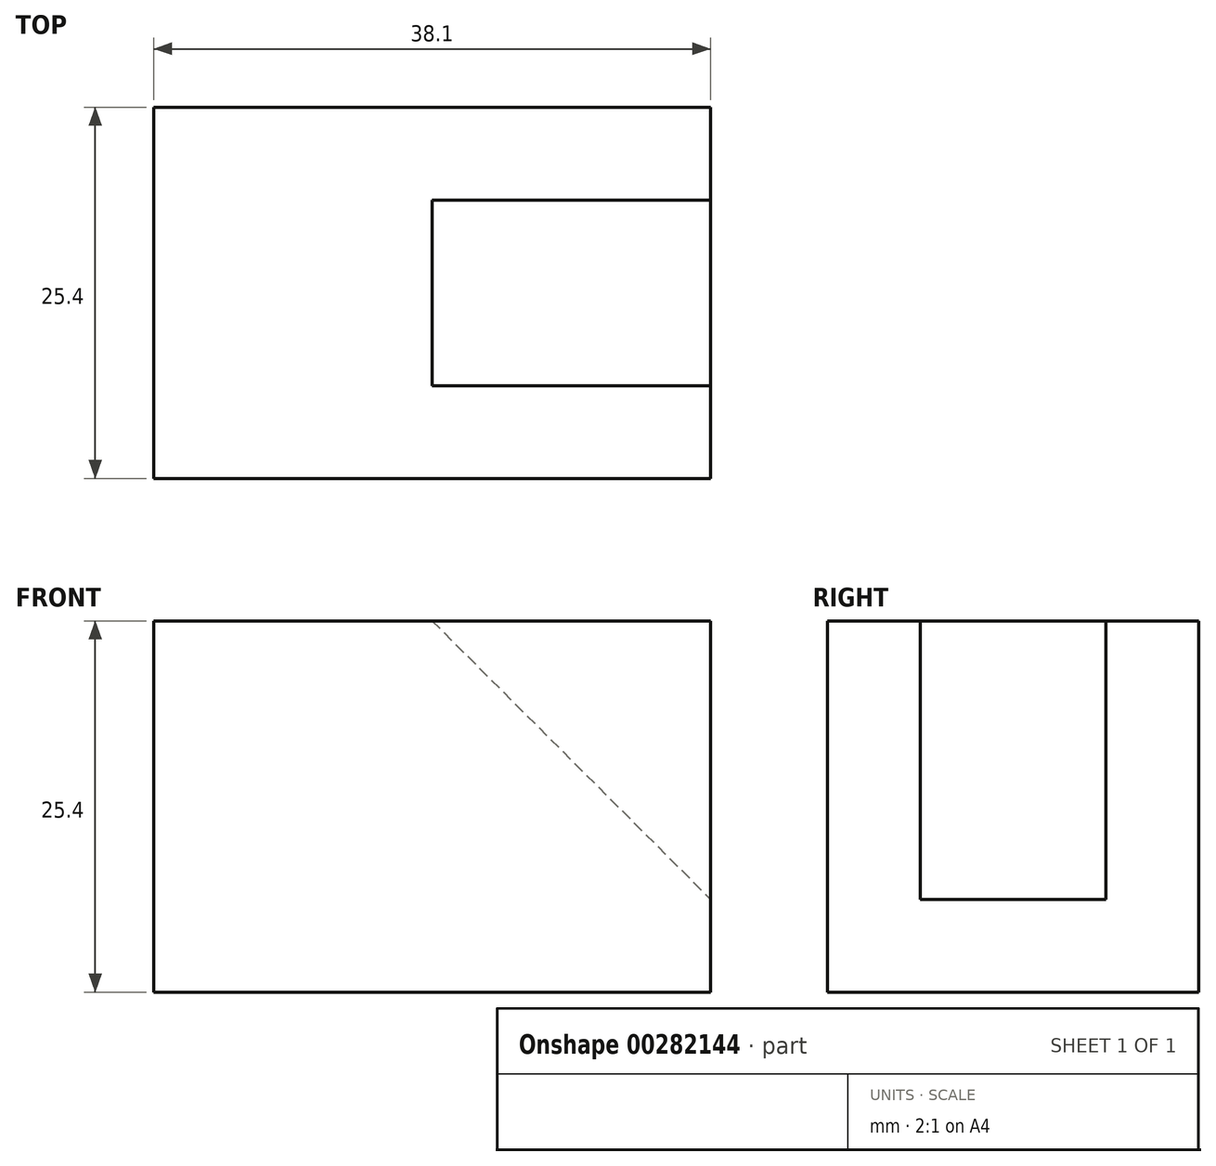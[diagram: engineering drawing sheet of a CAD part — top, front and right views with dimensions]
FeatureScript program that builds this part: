
annotation { "Feature Type Name" : "Feature", "Feature Type Description" : "" }
export const myFeature = defineFeature(function(context is Context, id is Id, definition is map)
    precondition{}
    {
        {
            var Q0;
            Q0=qCreatedBy(makeId("Front.planeOp"),FACE);
            var sketch = newSketch(context, id + "F0", { "sketchPlane" : qUnion([Q0])});
            skLineSegment(sketch, "E0.bottom", {"start": v(0, 0) * mm, "end": v(38.1, 0) * mm});
            skLineSegment(sketch, "E0.top", {"start": v(0, 25.4) * mm, "end": v(38.1, 25.4) * mm});
            skLineSegment(sketch, "E0.left", {"start": v(0, 0) * mm, "end": v(0, 25.4) * mm});
            skLineSegment(sketch, "E0.right", {"start": v(38.1, 0) * mm, "end": v(38.1, 25.4) * mm});
            skLineSegment(sketch, "E1", {"start": v(19.05, 25.4) * mm, "end": v(38.1, 6.35) * mm});
            skSolve(sketch);
        }
        {
            var Q0;
            {var subQ1=sQuery(id+"F0.wireOp",EDGE,"E0.bottom");Q0=makeQuery(id+"F0.imprint","IMPRINT",FACE,{"disambiguationData":[TD([[makeQuery(id+"F0.imprint","IMPRINT",EDGE,{"derivedFrom":subQ1}),1.0]])]});}
            var Q1;
            {var subQ3=sQuery(id+"F0.wireOp",EDGE,"E1");Q1=makeQuery(id+"F0.imprint","IMPRINT",FACE,{"disambiguationData":[TD([[makeQuery(id+"F0.imprint","IMPRINT",EDGE,{"derivedFrom":subQ3}),1.0]])]});}
            extrude(context, id + "F1", {"entities" : qUnion([Q0, Q1]), "endBound" : BoundingType.SYMMETRIC, "depth" : 25.4 * mm});
        }
        {
            var Q0;
            {var subQ3=sQuery(id+"F0.wireOp",EDGE,"E1");Q0=makeQuery(id+"F0.imprint","IMPRINT",FACE,{"disambiguationData":[TD([[makeQuery(id+"F0.imprint","IMPRINT",EDGE,{"derivedFrom":subQ3}),1.0]])]});}
            extrude(context, id + "F2", {"entities" : qUnion([Q0]), "operationType" : NewBodyOperationType.REMOVE, "endBound" : BoundingType.SYMMETRIC, "oppositeDirection" : true, "depth" : 12.7 * mm});
        }
    });
